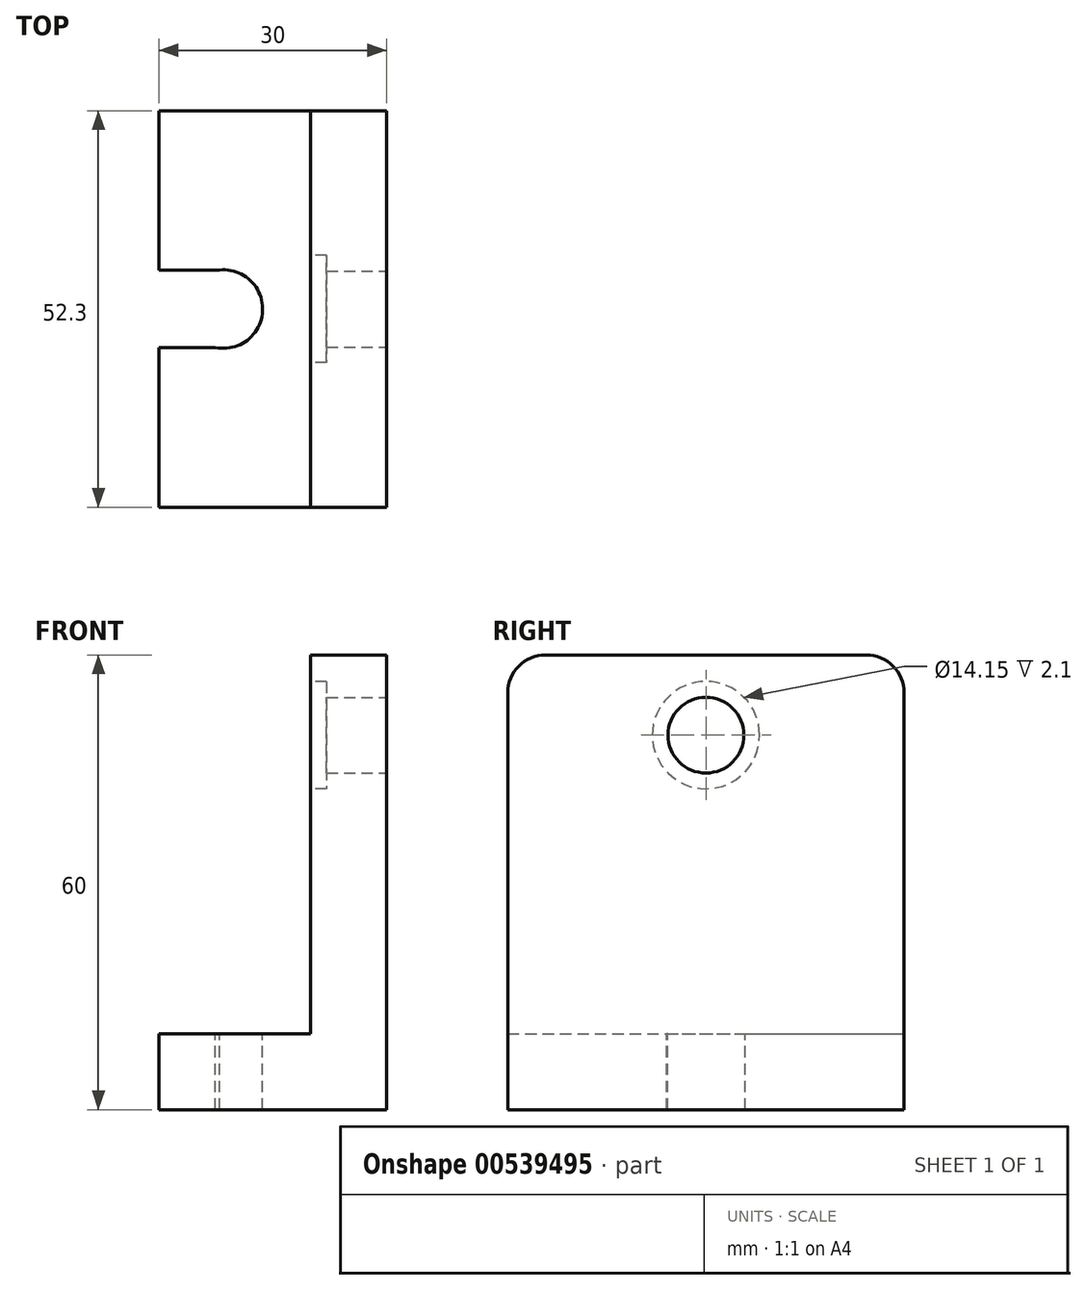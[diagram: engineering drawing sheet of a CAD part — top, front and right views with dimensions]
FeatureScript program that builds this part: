
annotation { "Feature Type Name" : "Feature", "Feature Type Description" : "" }
export const myFeature = defineFeature(function(context is Context, id is Id, definition is map)
    precondition{}
    {
        {
            var Q0;
            Q0=qCreatedBy(makeId("Front.planeOp"),FACE);
            var sketch = newSketch(context, id + "F0", { "sketchPlane" : qUnion([Q0])});
            skLineSegment(sketch, "E0", {"start": v(0, 60) * mm, "end": v(-10, 60) * mm});
            skLineSegment(sketch, "E1", {"start": v(-10, 60) * mm, "end": v(-10, 10) * mm});
            skLineSegment(sketch, "E2", {"start": v(-10, 10) * mm, "end": v(-30, 10) * mm});
            skLineSegment(sketch, "E3", {"start": v(-30, 10) * mm, "end": v(-30, 0) * mm});
            skLineSegment(sketch, "E4", {"start": v(-30, 0) * mm, "end": v(0, 0) * mm});
            skLineSegment(sketch, "E5", {"start": v(0, 0) * mm, "end": v(0, 60) * mm});
            skSolve(sketch);
        }
        {
            var Q0;
            Q0=makeQuery(id+"F0.imprint","IMPRINT",FACE,{"disambiguationData":[TD([[makeQuery(id+"F0.imprint","IMPRINT",EDGE,{"derivedFrom":sQuery(id+"F0.wireOp",EDGE,"E0")}),1.0]])]});
            extrude(context, id + "F1", {"entities" : qUnion([Q0]), "depth" : 52.3 * mm, "offsetDistance" : 25 * mm});
        }
        {
            var Q0;
            Q0=makeQuery(id+"F1.opExtrude","SWEPT_FACE",FACE,{"disambiguationData":[OSD([sQuery(id+"F0.wireOp",EDGE,"E5")])]});
            var sketch = newSketch(context, id + "F2", { "sketchPlane" : qUnion([Q0])});
            skCircle(sketch, "E6", {"center": v(-26.15, 49.42) * mm, "radius": 5 * mm});
            skPoint(sketch, "E6.centerSnap0", {"position": v(-26.15, 60) * mm});
            skSolve(sketch);
        }
        {
            var Q0;
            Q0=makeQuery(id+"F2.imprint","IMPRINT",FACE,{"disambiguationData":[TD([[makeQuery(id+"F2.imprint","IMPRINT",EDGE,{"derivedFrom":sQuery(id+"F2.wireOp",EDGE,"E6")}),1.0]])]});
            extrude(context, id + "F3", {"entities" : qUnion([Q0]), "operationType" : NewBodyOperationType.REMOVE, "endBound" : BoundingType.SYMMETRIC, "oppositeDirection" : true, "depth" : 25 * mm, "offsetDistance" : 25 * mm});
        }
        {
            var Q0;
            Q0=makeQuery(id+"F1.opExtrude","CAP_EDGE",EDGE,{"disambiguationData":[OSD([sQuery(id+"F0.wireOp",EDGE,"E0")])],"isStart":false});
            fillet(context, id + "F4", {"entities" : qUnion([Q0]), "radius" : 5 * mm, "tangentPropagation" : true, "allowEdgeOverflow" : false});
        }
        {
            var Q0;
            Q0=makeQuery(id+"F1.opExtrude","CAP_EDGE",EDGE,{"disambiguationData":[OSD([sQuery(id+"F0.wireOp",EDGE,"E0")])],"isStart":true});
            fillet(context, id + "F5", {"entities" : qUnion([Q0]), "radius" : 5 * mm, "tangentPropagation" : true, "allowEdgeOverflow" : false});
        }
        {
            var Q0;
            Q0=makeQuery(id+"F1.opExtrude","SWEPT_FACE",FACE,{"disambiguationData":[OSD([sQuery(id+"F0.wireOp",EDGE,"E1")])]});
            var sketch = newSketch(context, id + "F6", { "sketchPlane" : qUnion([Q0])});
            skCircle(sketch, "E7", {"center": v(26.15, 49.42) * mm, "radius": 7.07 * mm});
            skSolve(sketch);
        }
        {
            var Q0;
            Q0=makeQuery(id+"F6.imprint","IMPRINT",FACE,{"disambiguationData":[TD([[makeQuery(id+"F6.imprint","IMPRINT",EDGE,{"derivedFrom":sQuery(id+"F6.wireOp",EDGE,"E7")}),1.0]])]});
            var sketch = newSketch(context, id + "F7", { "sketchPlane" : qUnion([Q0])});
            skSolve(sketch);
        }
        {
            var Q0;
            Q0 = qSketchRegion(id + "F7", true);
            var Q1;
            Q1=makeQuery(id+"F6.imprint","IMPRINT",FACE,{"disambiguationData":[TD([[makeQuery(id+"F6.imprint","IMPRINT",EDGE,{"derivedFrom":sQuery(id+"F6.wireOp",EDGE,"E7")}),1.0]])]});
            extrude(context, id + "F8", {"entities" : qUnion([Q0, Q1]), "operationType" : NewBodyOperationType.REMOVE, "oppositeDirection" : true, "depth" : 2.1 * mm, "offsetDistance" : 25 * mm});
        }
        {
            var Q0;
            Q0=makeQuery(id+"F1.opExtrude","SWEPT_FACE",FACE,{"disambiguationData":[OSD([sQuery(id+"F0.wireOp",EDGE,"E2")])]});
            var sketch = newSketch(context, id + "F9", { "sketchPlane" : qUnion([Q0])});
            skCircle(sketch, "E8", {"center": v(-21.52, -26.15) * mm, "radius": 5.19 * mm});
            skPoint(sketch, "E8.centerSnap0", {"position": v(-30, -26.15) * mm});
            skLineSegment(sketch, "E9", {"start": v(-22.02, -20.99) * mm, "end": v(-30, -20.99) * mm});
            skLineSegment(sketch, "E10", {"start": v(-22.57, -31.23) * mm, "end": v(-30, -31.23) * mm});
            skLineSegment(sketch, "E11", {"start": v(-30, -31.23) * mm, "end": v(-30, -20.99) * mm});
            skSolve(sketch);
        }
        {
            var Q0;
            {var subQ0=sQuery(id+"F9.wireOp",EDGE,"E8");var subQ1=makeQuery(id+"F9.imprint","INTERSECT",VERTEX,{"derivedFrom":[subQ0,sQuery(id+"F9.wireOp",EDGE,"E9")]});Q0=makeQuery(id+"F9.imprint","IMPRINT",FACE,{"disambiguationData":[TD([[makeQuery(id+"F9.imprint","IMPRINT",EDGE,{"disambiguationData":[TD([[subQ1,-1.0]])],"derivedFrom":subQ0}),1.0]])]});}
            var Q1;
            {var subQ0=sQuery(id+"F9.wireOp",EDGE,"E9");Q1=makeQuery(id+"F9.imprint","IMPRINT",FACE,{"disambiguationData":[TD([[makeQuery(id+"F9.imprint","IMPRINT",EDGE,{"derivedFrom":subQ0}),1.0]])]});}
            extrude(context, id + "F10", {"entities" : qUnion([Q0, Q1]), "operationType" : NewBodyOperationType.REMOVE, "oppositeDirection" : true, "depth" : 25 * mm, "offsetDistance" : 25 * mm});
        }
        {
            var Q0;
            Q0=qCreatedBy(makeId("Front.planeOp"),FACE);
            cPlane(context, id + "F11", {"entities" : qUnion([Q0]), "cplaneType" : CPlaneType.OFFSET, "offset" : 25 * mm, "width" : 150 * mm, "height" : 150 * mm});
        }
    });
